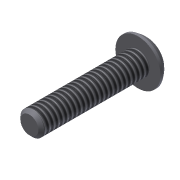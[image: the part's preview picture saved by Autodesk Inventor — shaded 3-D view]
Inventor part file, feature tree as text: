
AUTODESK INVENTOR PART (.ipt)
format: ipt  version: 2013 (Build 170138000, 138)  size: 116,224 bytes
history: native  units: in
note: dims shown in document units (in); Inventor stores cm internally (conversion verified against a paired STEP export)
features: sketch x3, extrude x2, revolve x1, chamfer x1, thread x1
ambient origin geometry x8: Origin, YZ Plane, XZ Plane, XY Plane, X Axis, Y Axis, Z Axis, Center Point
bodies: Solid1 (feature_tree)
feature tree (8):
  extrude  "Extrusion1"  Depth=0.75in TaperAngle=0.0deg
  revolve  "Revolution1"  [1 undecoded]
  extrude  "Extrusion2"  Depth=0.0938in
  chamfer  "Chamfer1"  Distance=0.0625in
  thread  "Thread1"  [1 undecoded]
  sketch  "Sketch1"  dims[d0=0.164in d1=0.75in d2=0.0in]
  sketch  "Sketch2"  dims[d3=0.087in d6=0.08in]
  sketch  "Sketch3"  dims[d7=90.0deg d8=0.0938in d9=0.0625in d10=0.0in d13=0.02in d14=0.125in d15=45.0deg d16=1.0in d17=0.0in d19=0.156in]
note: 2 required parameter values undecoded (feature->parameter linkage not recoverable at this tier; creation-order binding heuristic only, values carry confidence <= 0.55)